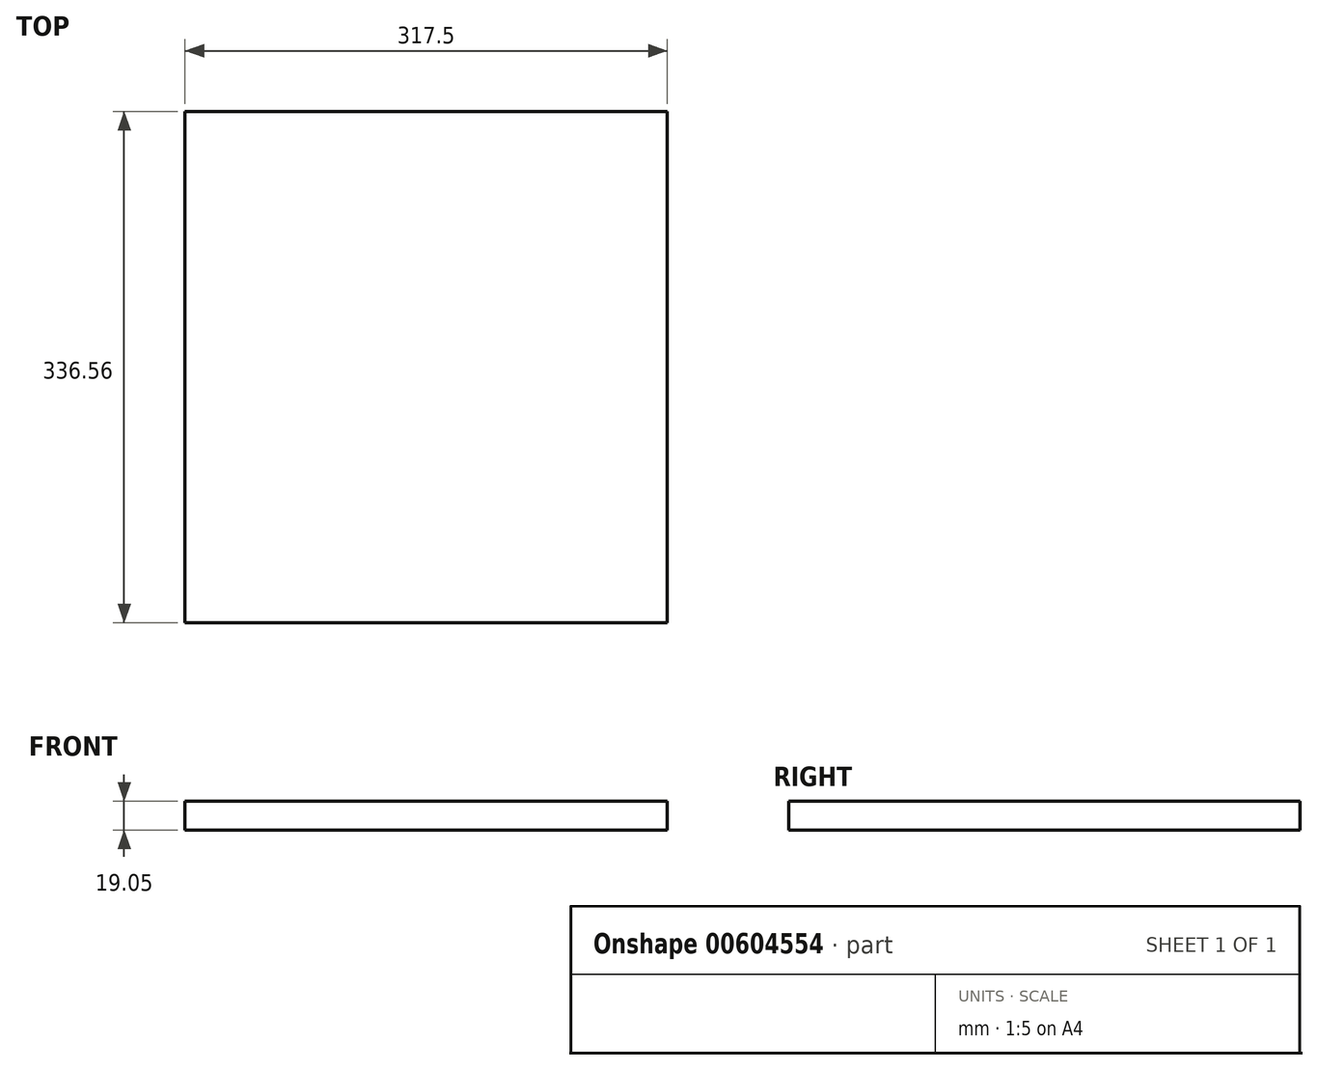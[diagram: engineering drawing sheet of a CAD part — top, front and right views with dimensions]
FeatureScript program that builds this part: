
annotation { "Feature Type Name" : "Feature", "Feature Type Description" : "" }
export const myFeature = defineFeature(function(context is Context, id is Id, definition is map)
    precondition{}
    {
        {
            var Q0;
            Q0=qCreatedBy(makeId("Top.planeOp"),FACE);
            var sketch = newSketch(context, id + "F0", { "sketchPlane" : qUnion([Q0])});
            skLineSegment(sketch, "E0.bottom", {"start": v(158.75, -168.27) * mm, "end": v(-158.75, -168.28) * mm});
            skLineSegment(sketch, "E0.top", {"start": v(158.75, 168.28) * mm, "end": v(-158.75, 168.27) * mm});
            skLineSegment(sketch, "E0.left", {"start": v(158.75, -168.27) * mm, "end": v(158.75, 168.28) * mm});
            skLineSegment(sketch, "E0.right", {"start": v(-158.75, -168.28) * mm, "end": v(-158.75, 168.28) * mm});
            skPoint(sketch, "E0.middle", {"position": v(0, 0) * mm});
            skSolve(sketch);
        }
        {
            var Q0;
            Q0=makeQuery(id+"F0.imprint","IMPRINT",FACE,{"disambiguationData":[TD([[makeQuery(id+"F0.imprint","IMPRINT",EDGE,{"derivedFrom":sQuery(id+"F0.wireOp",EDGE,"E0.bottom")}),-1.0]])]});
            extrude(context, id + "F1", {"entities" : qUnion([Q0]), "depth" : 19.05 * mm});
        }
    });
